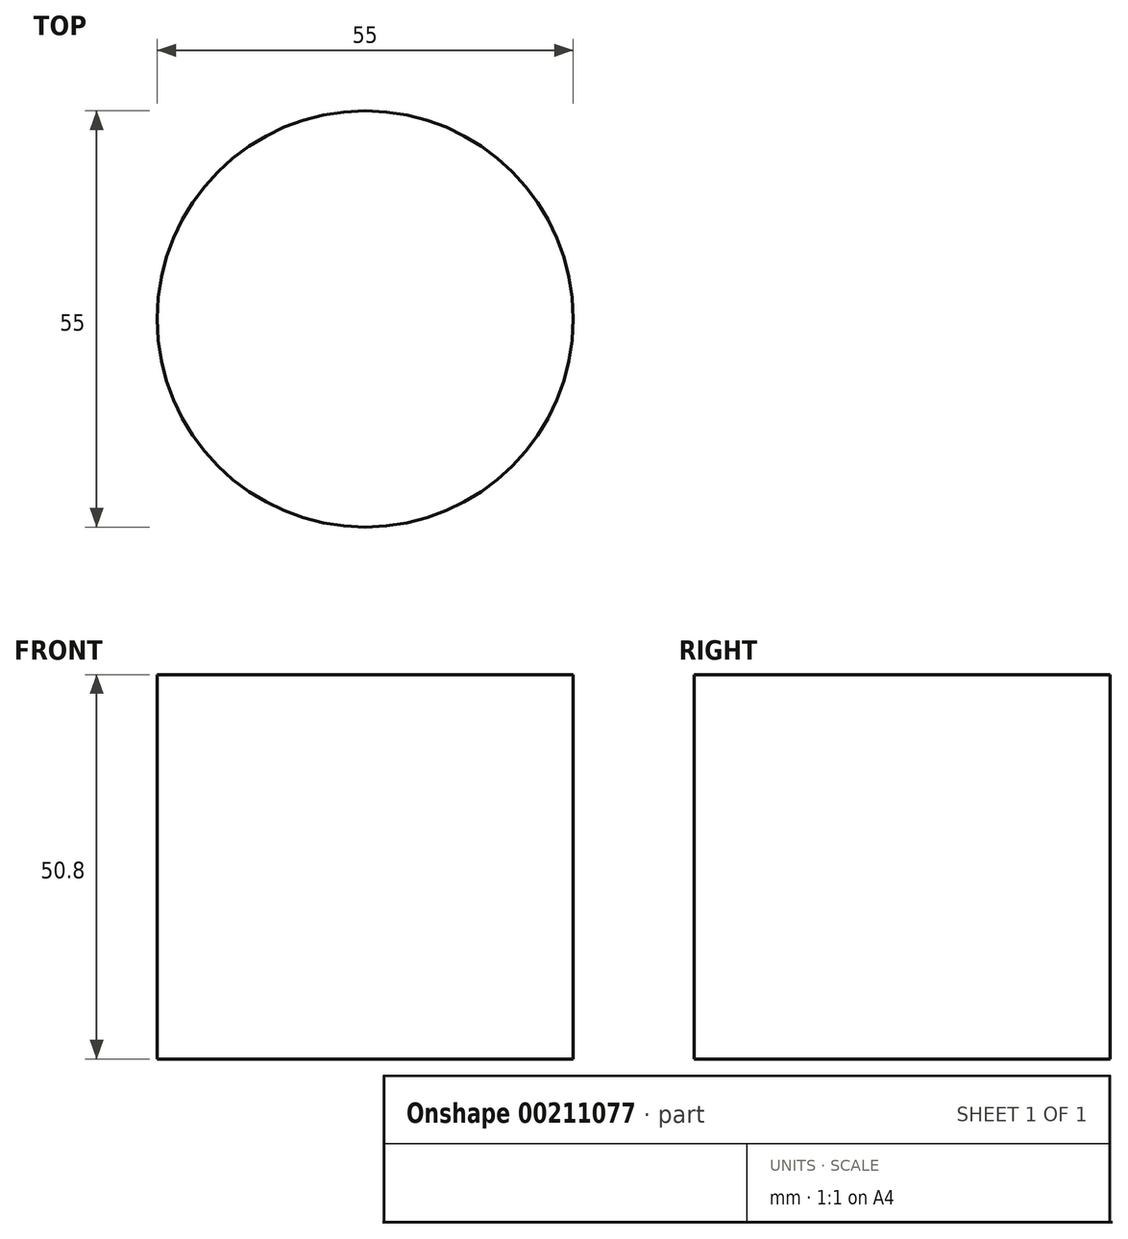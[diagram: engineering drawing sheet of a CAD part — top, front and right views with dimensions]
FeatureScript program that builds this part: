
annotation { "Feature Type Name" : "Feature", "Feature Type Description" : "" }
export const myFeature = defineFeature(function(context is Context, id is Id, definition is map)
    precondition{}
    {
        {
            var Q0;
            Q0=qCreatedBy(makeId("Top.planeOp"),FACE);
            var sketch = newSketch(context, id + "F0", { "sketchPlane" : qUnion([Q0])});
            skCircle(sketch, "E0", {"center": v(0, 0) * mm, "radius": 27.5 * mm});
            skSolve(sketch);
        }
        {
            var Q0;
            Q0 = qSketchRegion(id + "F0", true);
            extrude(context, id + "F1", {"entities" : qUnion([Q0]), "depth" : 50.8 * mm});
        }
    });
